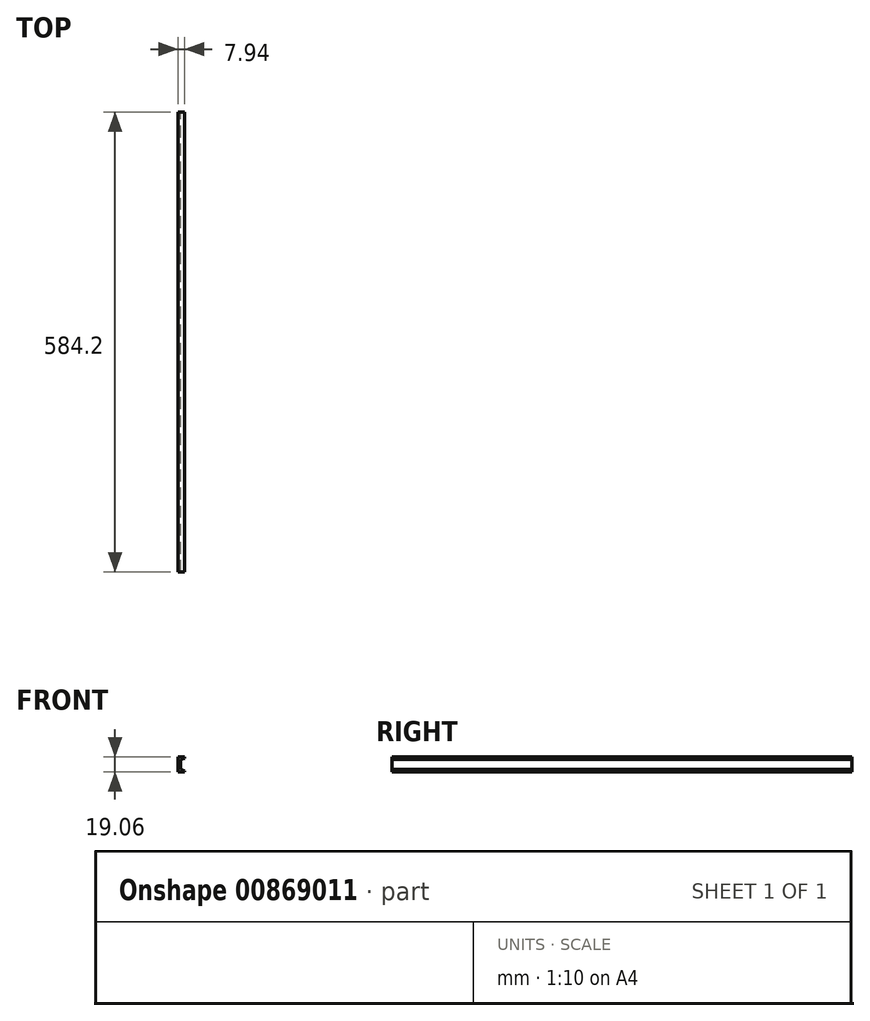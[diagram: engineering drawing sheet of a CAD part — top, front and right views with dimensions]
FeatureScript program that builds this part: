
annotation { "Feature Type Name" : "Feature", "Feature Type Description" : "" }
export const myFeature = defineFeature(function(context is Context, id is Id, definition is map)
    precondition{}
    {
        {
            var Q0;
            Q0=qCreatedBy(makeId("Front.planeOp"), FACE);
            var sketch = newSketch(context, id + "F0", { "sketchPlane" : qUnion([Q0])});
            skLineSegment(sketch, "E0", {"start": v(0, 9.53) * mm, "end": v(0, -9.53) * mm});
            skLineSegment(sketch, "E1", {"start": v(0, 9.53) * mm, "end": v(7.94, 9.53) * mm});
            skLineSegment(sketch, "E2", {"start": v(7.94, 9.53) * mm, "end": v(7.94, 7.94) * mm});
            skLineSegment(sketch, "E3", {"start": v(7.94, 7.94) * mm, "end": v(3.17, 6.35) * mm});
            skLineSegment(sketch, "E4", {"start": v(3.17, 6.35) * mm, "end": v(3.18, -6.35) * mm});
            skLineSegment(sketch, "E5", {"start": v(3.17, -6.35) * mm, "end": v(7.94, -7.94) * mm});
            skLineSegment(sketch, "E6", {"start": v(7.94, -7.94) * mm, "end": v(7.94, -9.53) * mm});
            skLineSegment(sketch, "E7", {"start": v(7.94, -9.52) * mm, "end": v(0, -9.53) * mm});
            skLineSegment(sketch, "E8", {"start": v(3.17, 6.35) * mm, "end": v(3.17, 9.53) * mm, "construction": true});
            skLineSegment(sketch, "E9", {"start": v(3.18, -6.35) * mm, "end": v(3.18, -9.53) * mm, "construction": true});
            skSolve(sketch);
        }
        {
            var Q0;
            Q0 = qSketchRegion(id + "F0", true);
            extrude(context, id + "F1", {"entities" : qUnion([Q0]), "depth" : 584.2 * mm, "offsetDistance" : 25.4 * mm, "symmetric" : true});
        }
    });
